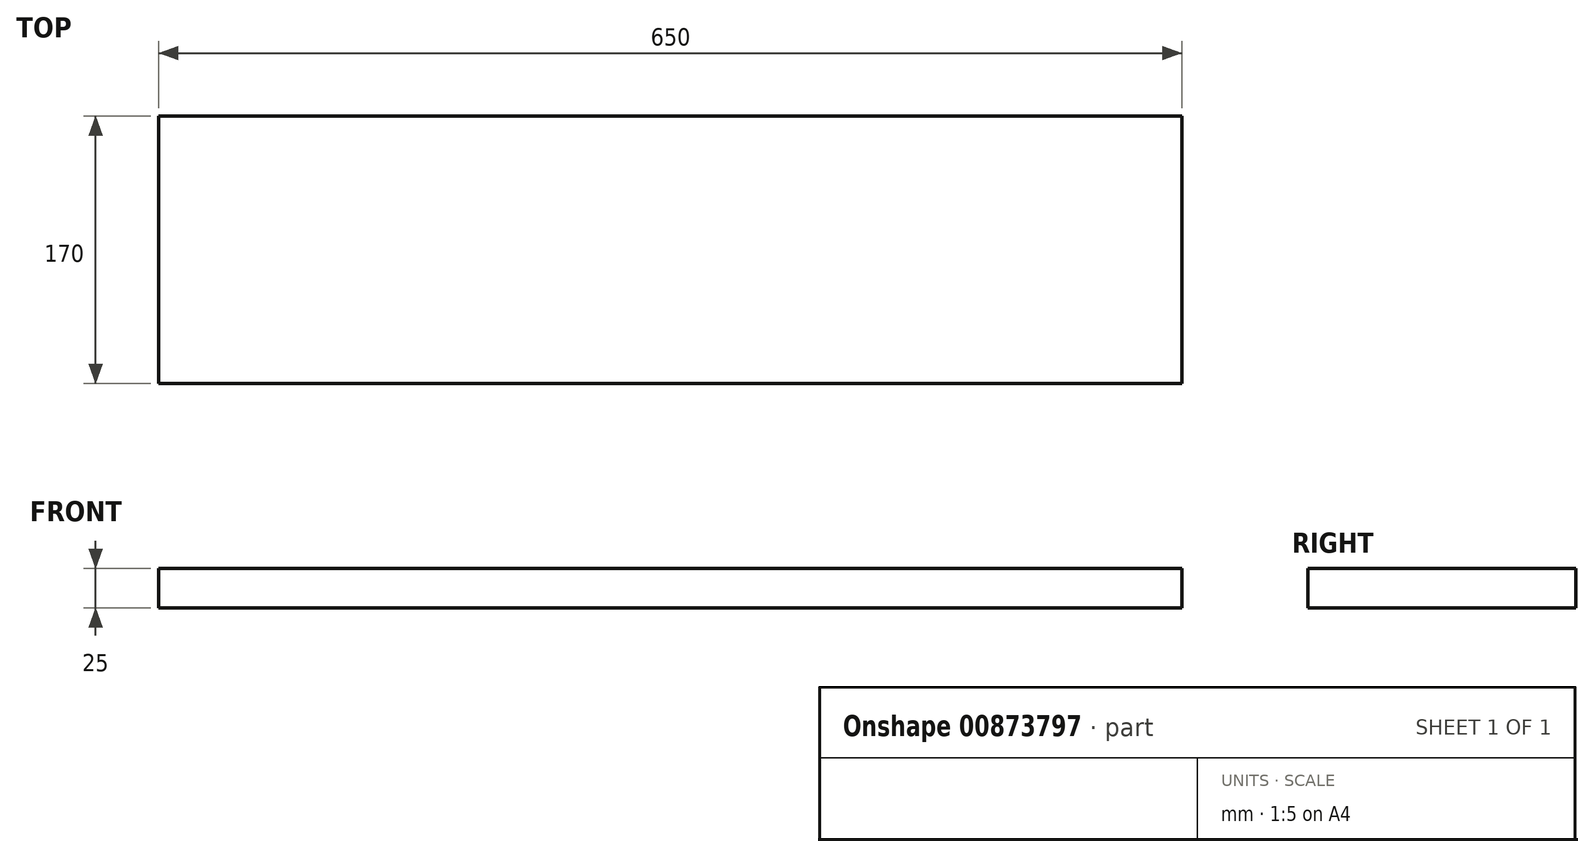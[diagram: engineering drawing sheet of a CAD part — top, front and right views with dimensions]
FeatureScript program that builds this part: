
annotation { "Feature Type Name" : "Feature", "Feature Type Description" : "" }
export const myFeature = defineFeature(function(context is Context, id is Id, definition is map)
    precondition{}
    {
        {
            var Q0;
            Q0=qCreatedBy(makeId("Top.planeOp"),FACE);
            var sketch = newSketch(context, id + "F0", { "sketchPlane" : qUnion([Q0])});
            skLineSegment(sketch, "E0.bottom", {"start": v(325, 85) * mm, "end": v(-325, 85) * mm});
            skLineSegment(sketch, "E0.top", {"start": v(325, -85) * mm, "end": v(-325, -85) * mm});
            skLineSegment(sketch, "E0.left", {"start": v(325, 85) * mm, "end": v(325, -85) * mm});
            skLineSegment(sketch, "E0.right", {"start": v(-325, 85) * mm, "end": v(-325, -85) * mm});
            skPoint(sketch, "E0.middle", {"position": v(0, 0) * mm});
            skLineSegment(sketch, "E1.bottom", {"start": v(-325, 85) * mm, "end": v(-55, 85) * mm});
            skLineSegment(sketch, "E1.top", {"start": v(-325, 235) * mm, "end": v(-55, 235) * mm});
            skLineSegment(sketch, "E1.left", {"start": v(-325, 85) * mm, "end": v(-325, 235) * mm});
            skLineSegment(sketch, "E1.right", {"start": v(-55, 85) * mm, "end": v(-55, 235) * mm});
            skLineSegment(sketch, "E2.bottom", {"start": v(325, 85) * mm, "end": v(135, 85) * mm});
            skLineSegment(sketch, "E2.top", {"start": v(325, 235) * mm, "end": v(135, 235) * mm});
            skLineSegment(sketch, "E2.left", {"start": v(325, 85) * mm, "end": v(325, 235) * mm});
            skLineSegment(sketch, "E2.right", {"start": v(135, 85) * mm, "end": v(135, 235) * mm});
            skSolve(sketch);
        }
        {
            var Q0;
            Q0=makeQuery(id+"F0.imprint","IMPRINT",FACE,{"disambiguationData":[TD([[makeQuery(id+"F0.imprint","IMPRINT",EDGE,{"derivedFrom":sQuery(id+"F0.wireOp",EDGE,"E1.bottom")}),1.0]])]});
            var Q1;
            Q1=makeQuery(id+"F0.imprint","IMPRINT",FACE,{"disambiguationData":[TD([[makeQuery(id+"F0.imprint","IMPRINT",EDGE,{"derivedFrom":sQuery(id+"F0.wireOp",EDGE,"E2.bottom")}),-1.0]])]});
            var Q2;
            Q2=makeQuery(id+"F0.imprint","IMPRINT",FACE,{"disambiguationData":[TD([[makeQuery(id+"F0.imprint","IMPRINT",EDGE,{"derivedFrom":sQuery(id+"F0.wireOp",EDGE,"E0.bottom")}),1.0]])]});
            extrude(context, id + "F1", {"entities" : qUnion([Q0, Q1, Q2]), "depth" : 25 * mm, "offsetDistance" : 25 * mm});
        }
    });
